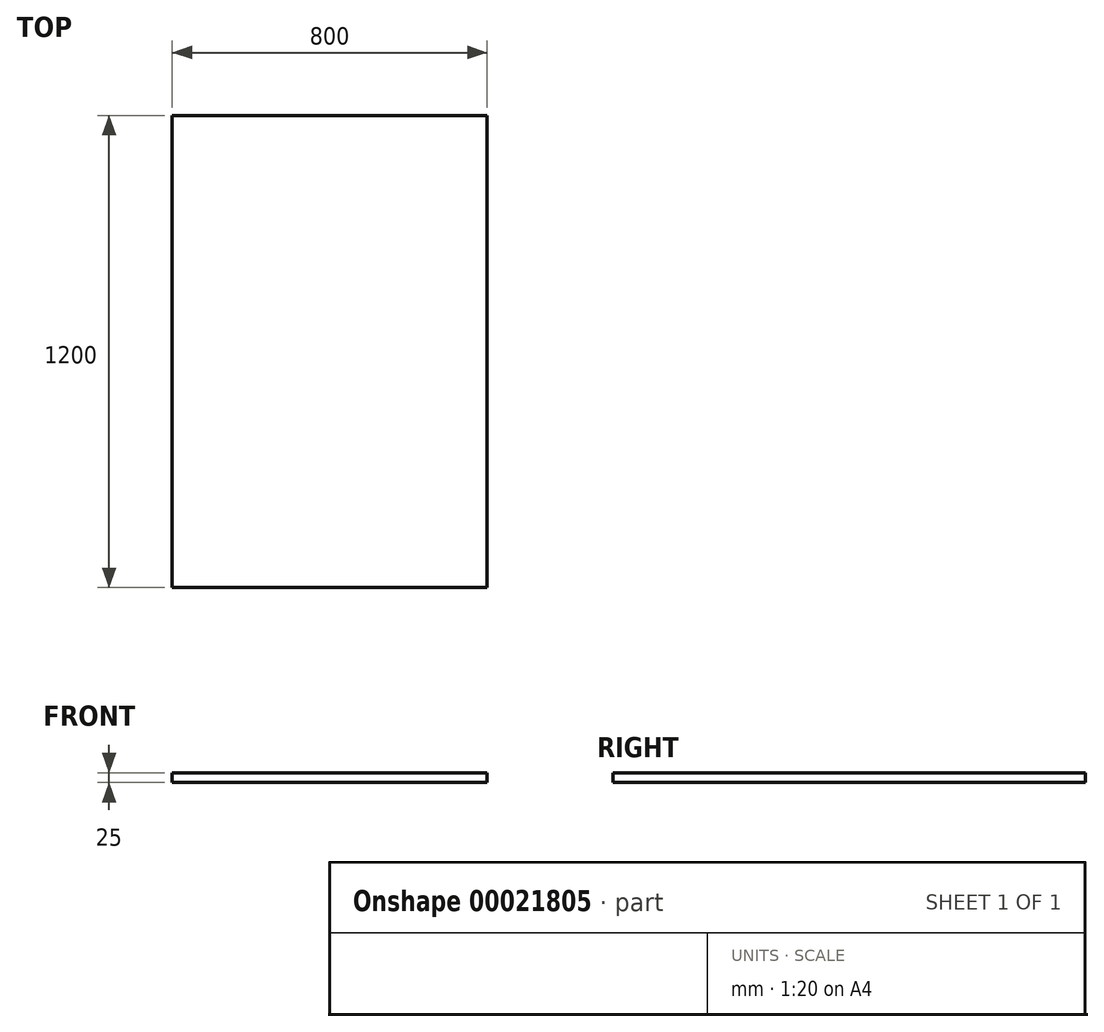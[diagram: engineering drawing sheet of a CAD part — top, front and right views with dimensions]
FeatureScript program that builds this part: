
annotation { "Feature Type Name" : "Feature", "Feature Type Description" : "" }
export const myFeature = defineFeature(function(context is Context, id is Id, definition is map)
    precondition{}
    {
        {
            var Q0;
            Q0=qCreatedBy(makeId("Top.planeOp"),FACE);
            var sketch = newSketch(context, id + "F0", { "sketchPlane" : qUnion([Q0])});
            skLineSegment(sketch, "E0.bottom", {"start": v(0, 0) * mm, "end": v(800, 0) * mm});
            skLineSegment(sketch, "E0.top", {"start": v(0, 1200) * mm, "end": v(800, 1200) * mm});
            skLineSegment(sketch, "E0.left", {"start": v(0, 0) * mm, "end": v(0, 1200) * mm});
            skLineSegment(sketch, "E0.right", {"start": v(800, 0) * mm, "end": v(800, 1200) * mm});
            skSolve(sketch);
        }
        {
            var Q0;
            Q0=makeQuery(id+"F0.imprint","IMPRINT",FACE,{"disambiguationData":[TD([[makeQuery(id+"F0.imprint","IMPRINT",EDGE,{"derivedFrom":sQuery(id+"F0.wireOp",EDGE,"E0.bottom")}),1.0]])]});
            extrude(context, id + "F1", {"entities" : qUnion([Q0]), "depth" : 25 * mm});
        }
    });
